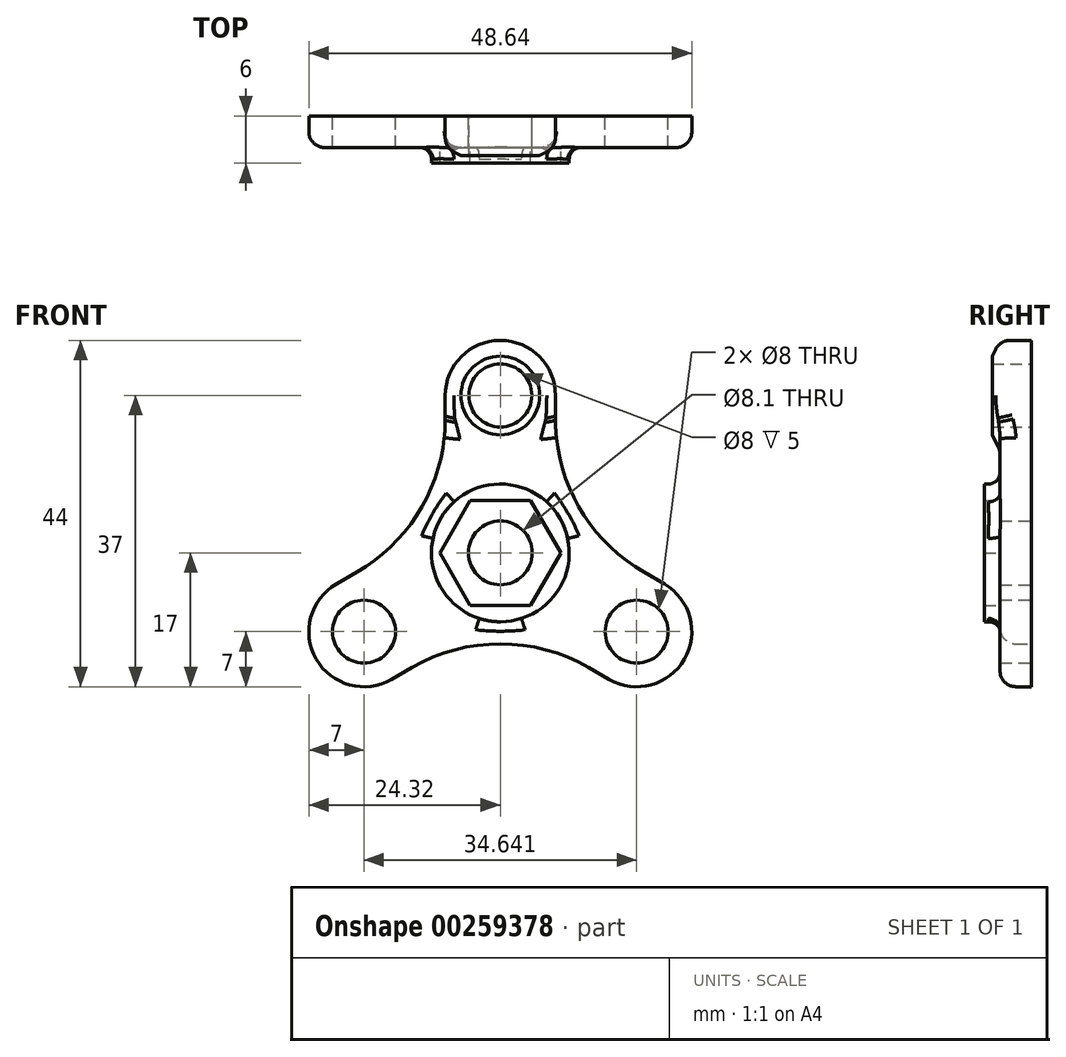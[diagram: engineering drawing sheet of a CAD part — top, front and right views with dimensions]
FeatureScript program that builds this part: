
annotation { "Feature Type Name" : "Feature", "Feature Type Description" : "" }
export const myFeature = defineFeature(function(context is Context, id is Id, definition is map)
    precondition{}
    {
        {
            var Q0;
            Q0=qCreatedBy(makeId("Front.planeOp"),FACE);
            var sketch = newSketch(context, id + "F0", { "sketchPlane" : qUnion([Q0])});
            skLineSegment(sketch, "E0", {"start": v(0, 20) * mm, "end": v(-17.32, -10) * mm, "construction": true});
            skLineSegment(sketch, "E1", {"start": v(-17.32, -10) * mm, "end": v(17.32, -10) * mm, "construction": true});
            skLineSegment(sketch, "E2", {"start": v(17.32, -10) * mm, "end": v(0, 20) * mm, "construction": true});
            skCircle(sketch, "E3", {"center": v(0, 0) * mm, "radius": 20 * mm, "construction": true});
            skCircle(sketch, "E4", {"center": v(0, 20) * mm, "radius": 4 * mm});
            skCircle(sketch, "E5", {"center": v(0, 20) * mm, "radius": 11 * mm, "construction": true});
            skCircle(sketch, "E6", {"center": v(0, 0) * mm, "radius": 4.05 * mm});
            skLineSegment(sketch, "E7", {"start": v(-7, 17) * mm, "end": v(-7, 27) * mm});
            skLineSegment(sketch, "E8", {"start": v(-7, 27) * mm, "end": v(7, 27) * mm});
            skLineSegment(sketch, "E9", {"start": v(7, 27) * mm, "end": v(7, 17) * mm});
            skLineSegment(sketch, "E10.1.0", {"start": v(-19.88, -19.56) * mm, "end": v(-26.88, -7.44) * mm});
            skLineSegment(sketch, "E10.1.1", {"start": v(-11.22, -14.56) * mm, "end": v(-19.88, -19.56) * mm});
            skLineSegment(sketch, "E10.1.2", {"start": v(-26.88, -7.44) * mm, "end": v(-18.22, -2.44) * mm});
            skLineSegment(sketch, "E10.2.0", {"start": v(26.88, -7.44) * mm, "end": v(19.88, -19.56) * mm});
            skLineSegment(sketch, "E10.2.1", {"start": v(18.22, -2.44) * mm, "end": v(26.88, -7.44) * mm});
            skLineSegment(sketch, "E10.2.2", {"start": v(19.88, -19.56) * mm, "end": v(11.22, -14.56) * mm});
            skCircle(sketch, "E11.1.0", {"center": v(-17.32, -10) * mm, "radius": 4 * mm});
            skCircle(sketch, "E11.2.0", {"center": v(17.32, -10) * mm, "radius": 4 * mm});
            skCircle(sketch, "E12", {"center": v(0, 0) * mm, "radius": 31 * mm, "construction": true});
            skArc(sketch, "E13", {"start": v(-18.22, -2.44) * mm, "mid": v(-10, 5.78) * mm, "end": v(-7, 17) * mm});
            skArc(sketch, "E14", {"start": v(7, 17) * mm, "mid": v(10, 5.78) * mm, "end": v(18.22, -2.44) * mm});
            skArc(sketch, "E15", {"start": v(11.22, -14.56) * mm, "mid": v(0, -11.56) * mm, "end": v(-11.22, -14.56) * mm});
            skSolve(sketch);
        }
        {
            var Q0;
            Q0 = qSketchRegion(id + "F0", true);
            extrude(context, id + "F1", {"entities" : qUnion([Q0]), "depth" : 4 * mm});
        }
        {
            var Q0;
            Q0=makeQuery(id+"F1.opExtrude","SWEPT_EDGE",EDGE,{"disambiguationData":[OSD([sQuery(id+"F0.wireOp",EDGE,"E10.1.0"),sQuery(id+"F0.wireOp",EDGE,"E10.1.1")])]});
            var Q1;
            Q1=makeQuery(id+"F1.opExtrude","SWEPT_EDGE",EDGE,{"disambiguationData":[OSD([sQuery(id+"F0.wireOp",EDGE,"E10.1.0"),sQuery(id+"F0.wireOp",EDGE,"E10.1.2")])]});
            var Q2;
            Q2=makeQuery(id+"F1.opExtrude","SWEPT_EDGE",EDGE,{"disambiguationData":[OSD([sQuery(id+"F0.wireOp",EDGE,"E7"),sQuery(id+"F0.wireOp",EDGE,"E8")])]});
            var Q3;
            Q3=makeQuery(id+"F1.opExtrude","SWEPT_EDGE",EDGE,{"disambiguationData":[OSD([sQuery(id+"F0.wireOp",EDGE,"E8"),sQuery(id+"F0.wireOp",EDGE,"E9")])]});
            var Q4;
            Q4=makeQuery(id+"F1.opExtrude","SWEPT_EDGE",EDGE,{"disambiguationData":[OSD([sQuery(id+"F0.wireOp",EDGE,"E10.2.0"),sQuery(id+"F0.wireOp",EDGE,"E10.2.1")])]});
            var Q5;
            Q5=makeQuery(id+"F1.opExtrude","SWEPT_EDGE",EDGE,{"disambiguationData":[OSD([sQuery(id+"F0.wireOp",EDGE,"E10.2.0"),sQuery(id+"F0.wireOp",EDGE,"E10.2.2")])]});
            fillet(context, id + "F2", {"entities" : qUnion([Q0, Q1, Q2, Q3, Q4, Q5]), "radius" : 7 * mm, "tangentPropagation" : true, "allowEdgeOverflow" : false});
        }
        {
            var Q0;
            Q0=makeQuery(id+"F1.opExtrude","CAP_FACE",FACE,{"disambiguationData":[OSD([sQuery(id+"F0.wireOp",EDGE,"E4"),sQuery(id+"F0.wireOp",EDGE,"E6"),sQuery(id+"F0.wireOp",EDGE,"E7"),sQuery(id+"F0.wireOp",EDGE,"E8"),sQuery(id+"F0.wireOp",EDGE,"E9"),sQuery(id+"F0.wireOp",EDGE,"E10.1.0"),sQuery(id+"F0.wireOp",EDGE,"E10.1.1"),sQuery(id+"F0.wireOp",EDGE,"E10.1.2"),sQuery(id+"F0.wireOp",EDGE,"E10.2.0"),sQuery(id+"F0.wireOp",EDGE,"E10.2.1"),sQuery(id+"F0.wireOp",EDGE,"E10.2.2"),sQuery(id+"F0.wireOp",EDGE,"E11.1.0"),sQuery(id+"F0.wireOp",EDGE,"E11.2.0"),sQuery(id+"F0.wireOp",EDGE,"E13"),sQuery(id+"F0.wireOp",EDGE,"E14"),sQuery(id+"F0.wireOp",EDGE,"E15")])],"isStart":false});
            var sketch = newSketch(context, id + "F3", { "sketchPlane" : qUnion([Q0])});
            skCircle(sketch, "E16.0", {"center": v(0, 20) * mm, "radius": 4 * mm});
            skCircle(sketch, "E17", {"center": v(0, 20) * mm, "radius": 7 * mm});
            skSolve(sketch);
        }
        {
            var Q0;
            Q0=makeQuery(id+"F3.imprint","IMPRINT",FACE,{"disambiguationData":[TD([[makeQuery(id+"F3.imprint","IMPRINT",EDGE,{"derivedFrom":sQuery(id+"F3.wireOp",EDGE,"E16.0")}),-1.0]])]});
            extrude(context, id + "F4", {"entities" : qUnion([Q0]), "operationType" : NewBodyOperationType.ADD, "depth" : 1 * mm});
        }
        {
            var Q0;
            Q0=makeQuery(id+"F4.opExtrude","CAP_EDGE",EDGE,{"disambiguationData":[OSD([sQuery(id+"F3.wireOp",EDGE,"E17")])],"isStart":false});
            chamfer(context, id + "F5", {"entities" : qUnion([Q0]), "chamferType" : ChamferType.TWO_OFFSETS, "width1" : 2 * mm, "oppositeDirection" : false, "width2" : 1 * mm, "tangentPropagation" : true});
        }
        {
            var Q0;
            Q0=makeQuery(id+"F5.opChamfer","BLEND_EDGE",EDGE,{"blendedFrom":[makeQuery(id+"F4.opExtrude","CAP_EDGE",EDGE,{"disambiguationData":[OSD([sQuery(id+"F3.wireOp",EDGE,"E17")])],"isStart":false}),makeQuery(id+"F1.opExtrude","CAP_FACE",FACE,{"disambiguationData":[OSD([sQuery(id+"F0.wireOp",EDGE,"E4"),sQuery(id+"F0.wireOp",EDGE,"E6"),sQuery(id+"F0.wireOp",EDGE,"E7"),sQuery(id+"F0.wireOp",EDGE,"E8"),sQuery(id+"F0.wireOp",EDGE,"E9"),sQuery(id+"F0.wireOp",EDGE,"E10.1.0"),sQuery(id+"F0.wireOp",EDGE,"E10.1.1"),sQuery(id+"F0.wireOp",EDGE,"E10.1.2"),sQuery(id+"F0.wireOp",EDGE,"E10.2.0"),sQuery(id+"F0.wireOp",EDGE,"E10.2.1"),sQuery(id+"F0.wireOp",EDGE,"E10.2.2"),sQuery(id+"F0.wireOp",EDGE,"E11.1.0"),sQuery(id+"F0.wireOp",EDGE,"E11.2.0"),sQuery(id+"F0.wireOp",EDGE,"E13"),sQuery(id+"F0.wireOp",EDGE,"E14"),sQuery(id+"F0.wireOp",EDGE,"E15")])],"isStart":false})],"blendedInto":[makeQuery(id+"F1.opExtrude","CAP_FACE",FACE,{"disambiguationData":[OSD([sQuery(id+"F0.wireOp",EDGE,"E4"),sQuery(id+"F0.wireOp",EDGE,"E6"),sQuery(id+"F0.wireOp",EDGE,"E7"),sQuery(id+"F0.wireOp",EDGE,"E8"),sQuery(id+"F0.wireOp",EDGE,"E9"),sQuery(id+"F0.wireOp",EDGE,"E10.1.0"),sQuery(id+"F0.wireOp",EDGE,"E10.1.1"),sQuery(id+"F0.wireOp",EDGE,"E10.1.2"),sQuery(id+"F0.wireOp",EDGE,"E10.2.0"),sQuery(id+"F0.wireOp",EDGE,"E10.2.1"),sQuery(id+"F0.wireOp",EDGE,"E10.2.2"),sQuery(id+"F0.wireOp",EDGE,"E11.1.0"),sQuery(id+"F0.wireOp",EDGE,"E11.2.0"),sQuery(id+"F0.wireOp",EDGE,"E13"),sQuery(id+"F0.wireOp",EDGE,"E14"),sQuery(id+"F0.wireOp",EDGE,"E15")])],"isStart":false})]});
            fillet(context, id + "F6", {"entities" : qUnion([Q0]), "radius" : 2.5 * mm, "tangentPropagation" : true, "allowEdgeOverflow" : false});
        }
        {
            var Q0;
            Q0=makeQuery(id+"F1.opExtrude","CAP_EDGE",EDGE,{"disambiguationData":[OSD([sQuery(id+"F0.wireOp",EDGE,"E15")])],"isStart":false});
            fillet(context, id + "F7", {"entities" : qUnion([Q0]), "radius" : 2 * mm, "tangentPropagation" : true, "allowEdgeOverflow" : false});
        }
        {
            var Q0;
            Q0=makeQuery(id+"F1.opExtrude","CAP_FACE",FACE,{"disambiguationData":[OSD([sQuery(id+"F0.wireOp",EDGE,"E4"),sQuery(id+"F0.wireOp",EDGE,"E6"),sQuery(id+"F0.wireOp",EDGE,"E7"),sQuery(id+"F0.wireOp",EDGE,"E8"),sQuery(id+"F0.wireOp",EDGE,"E9"),sQuery(id+"F0.wireOp",EDGE,"E10.1.0"),sQuery(id+"F0.wireOp",EDGE,"E10.1.1"),sQuery(id+"F0.wireOp",EDGE,"E10.1.2"),sQuery(id+"F0.wireOp",EDGE,"E10.2.0"),sQuery(id+"F0.wireOp",EDGE,"E10.2.1"),sQuery(id+"F0.wireOp",EDGE,"E10.2.2"),sQuery(id+"F0.wireOp",EDGE,"E11.1.0"),sQuery(id+"F0.wireOp",EDGE,"E11.2.0"),sQuery(id+"F0.wireOp",EDGE,"E13"),sQuery(id+"F0.wireOp",EDGE,"E14"),sQuery(id+"F0.wireOp",EDGE,"E15")])],"isStart":false});
            var sketch = newSketch(context, id + "F8", { "sketchPlane" : qUnion([Q0])});
            skCircle(sketch, "E18.0", {"center": v(-17.32, -10) * mm, "radius": 4 * mm, "construction": true});
            skCircle(sketch, "E19.0", {"center": v(0, 20) * mm, "radius": 4 * mm, "construction": true});
            skCircle(sketch, "E20.0", {"center": v(17.32, -10) * mm, "radius": 4 * mm, "construction": true});
            skCircle(sketch, "E21", {"center": v(0, 20) * mm, "radius": 11 * mm, "construction": true});
            skCircle(sketch, "E22", {"center": v(0, 0) * mm, "radius": 8.75 * mm});
            skCircle(sketch, "E23.cCircle", {"center": v(0, 0) * mm, "radius": 6.65 * mm, "construction": true});
            skLineSegment(sketch, "E23.0", {"start": v(-3.84, 6.65) * mm, "end": v(3.84, 6.65) * mm});
            skLineSegment(sketch, "E23.1", {"start": v(3.84, 6.65) * mm, "end": v(7.68, 0) * mm});
            skLineSegment(sketch, "E23.2", {"start": v(7.68, 0) * mm, "end": v(3.84, -6.65) * mm});
            skLineSegment(sketch, "E23.3", {"start": v(3.84, -6.65) * mm, "end": v(-3.84, -6.65) * mm});
            skLineSegment(sketch, "E23.4", {"start": v(-3.84, -6.65) * mm, "end": v(-7.68, 0) * mm});
            skLineSegment(sketch, "E23.5", {"start": v(-7.68, 0) * mm, "end": v(-3.84, 6.65) * mm});
            skPoint(sketch, "E23.0.midPoint", {"position": v(0, 6.65) * mm});
            skSolve(sketch);
        }
        {
            var Q0;
            Q0=makeQuery(id+"F8.imprint","IMPRINT",FACE,{"disambiguationData":[TD([[makeQuery(id+"F8.imprint","IMPRINT",EDGE,{"derivedFrom":sQuery(id+"F8.wireOp",EDGE,"E22")}),1.0]])]});
            extrude(context, id + "F9", {"entities" : qUnion([Q0]), "operationType" : NewBodyOperationType.ADD, "depth" : 2 * mm});
        }
        {
            var Q0;
            Q0=makeQuery(id+"F9.opExtrude","CAP_EDGE",EDGE,{"disambiguationData":[OSD([sQuery(id+"F8.wireOp",EDGE,"E22")])],"isStart":true});
            fillet(context, id + "F10", {"entities" : qUnion([Q0]), "radius" : 1.5 * mm, "tangentPropagation" : true, "allowEdgeOverflow" : false});
        }
    });
